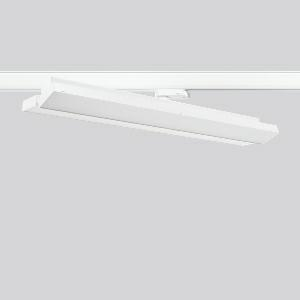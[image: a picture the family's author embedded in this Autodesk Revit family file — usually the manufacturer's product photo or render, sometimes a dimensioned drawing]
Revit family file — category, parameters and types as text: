
# Revit family: tx-move_742164_002_1_76_efca
name_source: partatom
category: Lighting Fixtures
units: mm (PartAtom-declared; Revit-internal decimal feet)

## family parameters
Cut with Voids When Loaded = No
Host = Face
Light Source = No
Part Type = Normal
Room Calculation Point = No
Round Connector Dimension = Use Diameter
Shared = No

## types (1)
- MultiLumen 1 (1 x LED Modul 840, 2625 lm, 4000)
    Apparent Load = 41 VA
    CIE Flux Codes = 47 79 96 100 100
    Color Rendering = 80
    Color Temperature = 4000
    Default Elevation = 1800 mm
    Description = Series: TX-MOVE
Multifunctional surface-mounted spotlight for area lighting. Very flat design. Housing: sheet steel, powder-coated. Rotation range: 356°. Swivel range: 90°. Consistent alignment possible with visible tilt scale. High-efficiency LED units with flush-mounted opal diffuser made of non-yellowing PMMA. Symmetrical wide beam light emission. With adapter for RZB 3-circuit DALI tracks. Suitable for Track on ceiling. MultiLumen: Luminous flux adjustable in 3 steps. Factory setting is the highest luminous flux. Environmentally friendly and resource-saving due to replaceable and recyclable components. 
Colour: traffic white, matt (RAL 9016)
Length: 570 mm
Width: 119 mm
Height: 88 mm
Lamp: LED
Socket: without socket
Colour temperature: 4000K
Colour rendering index (CRI): 80
System power: 41 W
Rated luminous flux: 5250 lm
Luminous efficiency: 128 lm/W
System power 2: 57 W
Rated luminous flux 2: 7150 lm
Luminous efficiency 2: 125 lm/W
System power 3: 73 W
Rated luminous flux 3: 8750 lm
Luminous efficiency 3: 120 lm/W
Control gear: Dimmable EVG, DALI
Protection class: I
Type of protection: IP 20
    Height = 75 mm
    Lamp = 1 x LED Modul 840
    Lamp Light Flux = 2625 lm
    Lamp count = 1
    Length = 569 mm
    Lifetime = 50000 h
    Luminous efficacy = 128 lm/W
    Manufacturer = RZB
    ModVariant = No
    Model = 742164.002.1.76
    Mounting Place = Ceiling
    Mounting Type = Surface mounted
    Number of Poles = 1
    OnlyDefault = Yes
    Power Factor = 1
    Product Name = TX-MOVE
    Product group = Track mounted projectors
    ProductGroupID = 301
    Protection Class = Protection class I
    Protection Degree = IP 20
    RLX_Detail_Level = 1
    RLX_Emergency_Light_Flux = 0 lm
    RLX_Emergency_Type = 0
    RLX_Emergency_Type_DB = No
    RlxData = <blob elided: 29921 chars, md5=f289671f>
    Socket = socket
    Standby Power = 0 W
    System Light Flux = 5250 lm
    System Power = 41 W
    Type Comments = MultiLumen 1
    Type Image = 742164.002.jpg
    URL = http://relux.com
    VarID = multilumen_1
    Voltage = 0 V
    Weight = 0.00 kg
    Width = 119 mm

## geometry (parser evidence)
native form markers: Blend x4, Sweep x17
no freeform markers — native parametric forms only
